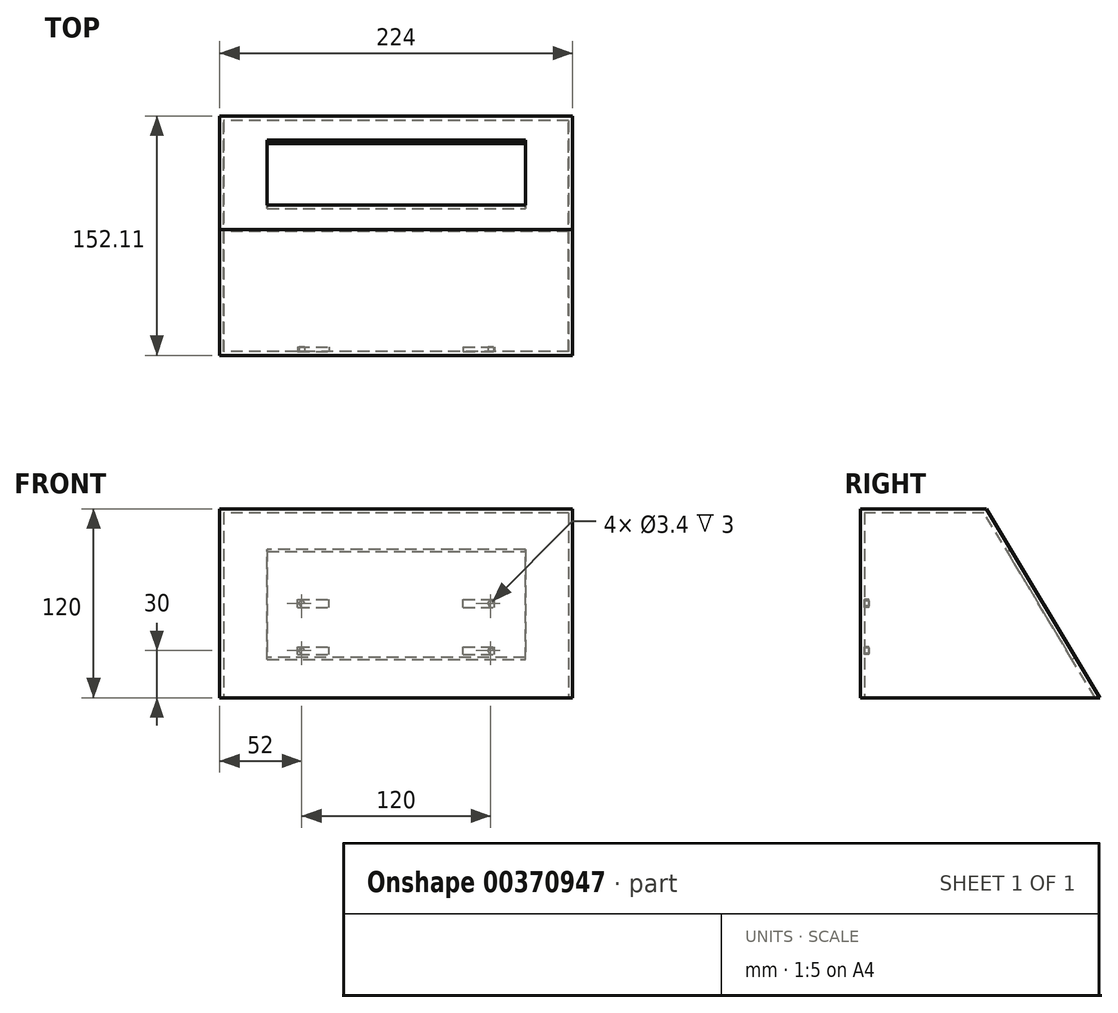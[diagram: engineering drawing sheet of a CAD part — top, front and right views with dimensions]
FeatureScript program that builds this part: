
annotation { "Feature Type Name" : "Feature", "Feature Type Description" : "" }
export const myFeature = defineFeature(function(context is Context, id is Id, definition is map)
    precondition{}
    {
        {
            var Q0;
            Q0=qCreatedBy(makeId("Right.planeOp"),FACE);
            var sketch = newSketch(context, id + "F0", { "sketchPlane" : qUnion([Q0])});
            skLineSegment(sketch, "E0", {"start": v(0, 0) * mm, "end": v(152.11, 0) * mm});
            skLineSegment(sketch, "E1", {"start": v(152.11, 0) * mm, "end": v(80, 120) * mm});
            skLineSegment(sketch, "E2", {"start": v(0, 120) * mm, "end": v(0, 0) * mm});
            skLineSegment(sketch, "E3", {"start": v(80, 120) * mm, "end": v(0, 120) * mm});
            skSolve(sketch);
        }
        {
            var Q0;
            Q0 = qSketchRegion(id + "F0", true);
            extrude(context, id + "F1", {"entities" : qUnion([Q0]), "depth" : 224 * mm});
        }
        {
            var Q0;
            Q0=makeQuery(id+"F1.opExtrude","SWEPT_FACE",FACE,{"disambiguationData":[OSD([sQuery(id+"F0.wireOp",EDGE,"E0")])]});
            shell(context, id + "F2", {"entities" : qUnion([Q0]), "thickness" : 2.5 * mm});
        }
        {
            var Q0;
            Q0=makeQuery(id+"F1.opExtrude","SWEPT_FACE",FACE,{"disambiguationData":[OSD([sQuery(id+"F0.wireOp",EDGE,"E1")])]});
            var sketch = newSketch(context, id + "F3", { "sketchPlane" : qUnion([Q0])});
            skLineSegment(sketch, "E4.bottom", {"start": v(-194, 31.65) * mm, "end": v(-30, 31.65) * mm});
            skLineSegment(sketch, "E4.top", {"start": v(-194, -48.35) * mm, "end": v(-30, -48.35) * mm});
            skLineSegment(sketch, "E4.left", {"start": v(-194, 31.65) * mm, "end": v(-194, -48.35) * mm});
            skLineSegment(sketch, "E4.right", {"start": v(-30, 31.65) * mm, "end": v(-30, -48.35) * mm});
            skSolve(sketch);
        }
        {
            var Q0;
            Q0 = qSketchRegion(id + "F3", true);
            extrude(context, id + "F4", {"entities" : qUnion([Q0]), "operationType" : NewBodyOperationType.REMOVE, "oppositeDirection" : true, "depth" : 6 * mm});
        }
        {
            var Q0;
            Q0=makeQuery(id+"F2.opShell","OFFSET_FACE",FACE,{"disambiguationData":[OSD([sQuery(id+"F0.wireOp",EDGE,"E2")])]});
            var sketch = newSketch(context, id + "F5", { "sketchPlane" : qUnion([Q0])});
            skCircle(sketch, "E5", {"center": v(-172, 30) * mm, "radius": 1.7 * mm});
            skCircle(sketch, "E6.0.1.0", {"center": v(-172, 60) * mm, "radius": 1.7 * mm});
            skCircle(sketch, "E6.1.0.0", {"center": v(-52, 30) * mm, "radius": 1.7 * mm});
            skCircle(sketch, "E6.1.1.0", {"center": v(-52, 60) * mm, "radius": 1.7 * mm});
            skLineSegment(sketch, "E6.direction1", {"start": v(-172, 30) * mm, "end": v(-52, 30) * mm, "construction": true});
            skLineSegment(sketch, "E6.direction2", {"start": v(-172, 30) * mm, "end": v(-172, 60) * mm, "construction": true});
            skLineSegment(sketch, "E7.bottom", {"start": v(-154.5, 27.5) * mm, "end": v(-174.5, 27.5) * mm});
            skLineSegment(sketch, "E7.top", {"start": v(-154.5, 32.5) * mm, "end": v(-174.5, 32.5) * mm});
            skLineSegment(sketch, "E7.left", {"start": v(-154.5, 27.5) * mm, "end": v(-154.5, 32.5) * mm});
            skLineSegment(sketch, "E7.right", {"start": v(-174.5, 27.5) * mm, "end": v(-174.5, 32.5) * mm});
            skLineSegment(sketch, "E8.0.1.0", {"start": v(-174.5, 57.5) * mm, "end": v(-174.5, 62.5) * mm});
            skLineSegment(sketch, "E8.0.1.1", {"start": v(-154.5, 62.5) * mm, "end": v(-174.5, 62.5) * mm});
            skLineSegment(sketch, "E8.0.1.2", {"start": v(-154.5, 57.5) * mm, "end": v(-154.5, 62.5) * mm});
            skLineSegment(sketch, "E8.0.1.3", {"start": v(-154.5, 57.5) * mm, "end": v(-174.5, 57.5) * mm});
            skLineSegment(sketch, "E8.1.0.0", {"start": v(-69.5, 27.5) * mm, "end": v(-69.5, 32.5) * mm});
            skLineSegment(sketch, "E8.1.0.1", {"start": v(-49.5, 32.5) * mm, "end": v(-69.5, 32.5) * mm});
            skLineSegment(sketch, "E8.1.0.2", {"start": v(-49.5, 27.5) * mm, "end": v(-49.5, 32.5) * mm});
            skLineSegment(sketch, "E8.1.0.3", {"start": v(-49.5, 27.5) * mm, "end": v(-69.5, 27.5) * mm});
            skLineSegment(sketch, "E8.1.1.0", {"start": v(-69.5, 57.5) * mm, "end": v(-69.5, 62.5) * mm});
            skLineSegment(sketch, "E8.1.1.1", {"start": v(-49.5, 62.5) * mm, "end": v(-69.5, 62.5) * mm});
            skLineSegment(sketch, "E8.1.1.2", {"start": v(-49.5, 57.5) * mm, "end": v(-49.5, 62.5) * mm});
            skLineSegment(sketch, "E8.1.1.3", {"start": v(-49.5, 57.5) * mm, "end": v(-69.5, 57.5) * mm});
            skLineSegment(sketch, "E8.direction1", {"start": v(-174.5, 27.5) * mm, "end": v(-69.5, 27.5) * mm, "construction": true});
            skLineSegment(sketch, "E8.direction2", {"start": v(-174.5, 27.5) * mm, "end": v(-174.5, 57.5) * mm, "construction": true});
            skSolve(sketch);
        }
        {
            var Q0;
            Q0 = qSketchRegion(id + "F5", true);
            extrude(context, id + "F6", {"entities" : qUnion([Q0]), "operationType" : NewBodyOperationType.ADD, "depth" : 3 * mm});
        }
    });
